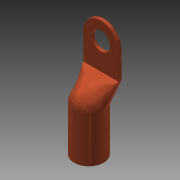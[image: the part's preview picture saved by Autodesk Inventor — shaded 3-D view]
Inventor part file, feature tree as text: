
AUTODESK INVENTOR PART (.ipt)
format: ipt  version: 2014 (Build 180170000, 170)  size: 400,896 bytes
history: native  units: in
note: dims shown in document units (in); Inventor stores cm internally (conversion verified against a paired STEP export)
features: sketch x6, fillet x5, extrude x3, other x3, plane x2, revolve x2, projected_geometry x2, split x1, loft x1, chamfer x1
ambient origin geometry x8: Origin, YZ Plane, XZ Plane, XY Plane, X Axis, Y Axis, Z Axis, Center Point
bodies: Solid1 (feature_tree)
feature tree (26):
  extrude  "Extrusion1"  Depth=0.75in
  plane  "Work Plane1"
  sketch  "Sketch2"  dims[d2=0.0625in d3=0.0in d4=0.125in]
  plane  "Work Plane2"
  revolve  "Revolution1"  [1 undecoded]
  split  "Split1"
  loft  "Loft1"
  fillet  "Fillet5"  Radius=0.5625in
  fillet  "Fillet6"  [1 undecoded]
  fillet  "Fillet7"  [1 undecoded]
  fillet  "Fillet8"  Radius=0.75in
  fillet  "Fillet9"  Radius=0.15in
  extrude  "Extrusion2"  Depth=0.25in
  revolve  "Revolution2"  [1 undecoded]
  chamfer  "Chamfer2"  Distance=0.875in
  sketch  "Sketch1"  dims[d0=0.375in d1=0.75in]
  sketch  "Sketch3"  dims[d5=0.625in d6=90.0deg d7=0.5625in d8=0.0in d9=0.0in d10=90.0deg d11=0.0in d12=90.0deg d17=0.75in d18=0.15in]
  sketch  "Sketch4"  dims[d22=0.01in d23=0.25in]
  other  "Srf1"
  other  "Edges1"
  other  "Edges2"
  sketch  "Sketch6"  dims[d24=0.25in d25=0.0625in d26=0.875in d27=0.0in]
  projected_geometry  "Projected Loop1"
  sketch  "Sketch7"  dims[d28=90.0deg d29=0.005in d30=0.125in d31=45.0deg]
  projected_geometry  "Projected Loop2"
  extrude  "ExtrusionSrf1"  Depth=0.005in TaperAngle=45.0deg
note: 4 required parameter values undecoded (feature->parameter linkage not recoverable at this tier; creation-order binding heuristic only, values carry confidence <= 0.55)